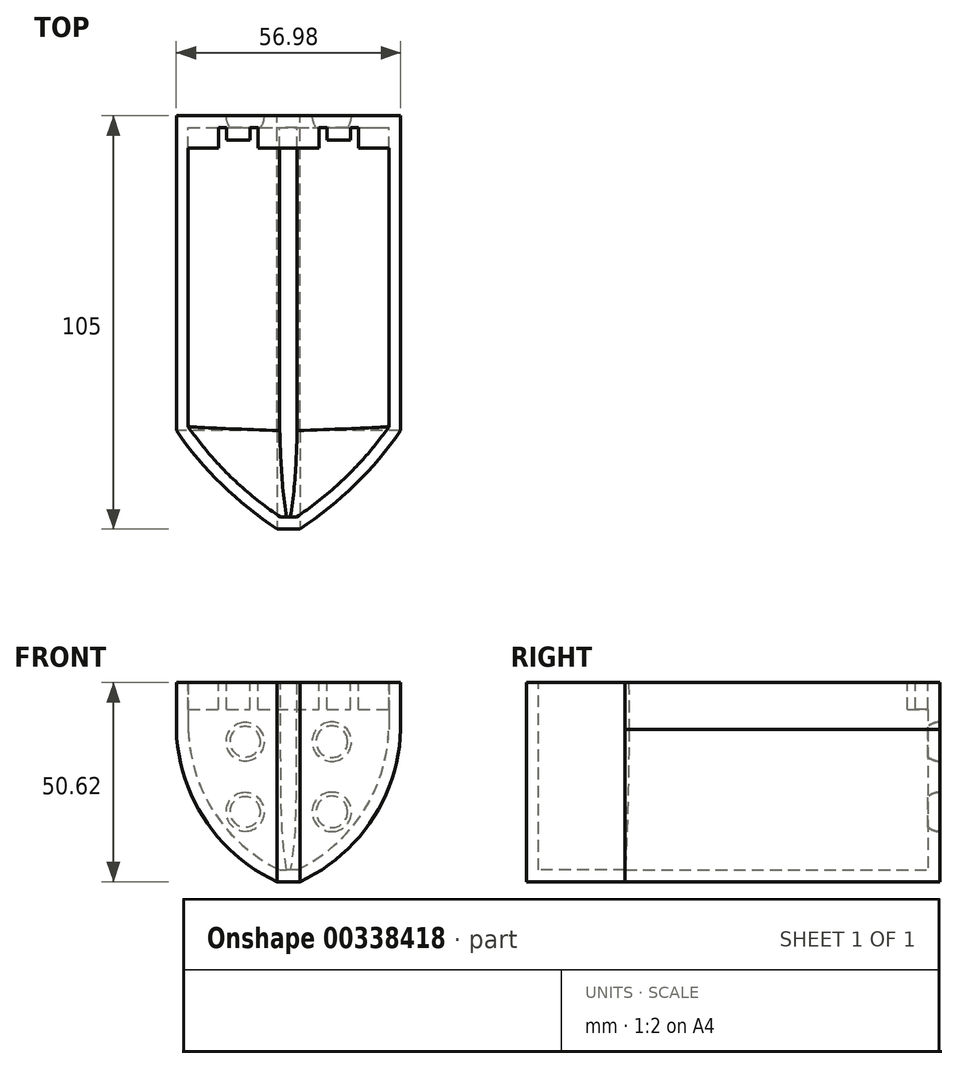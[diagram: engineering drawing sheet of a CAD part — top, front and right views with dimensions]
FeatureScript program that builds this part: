
annotation { "Feature Type Name" : "Feature", "Feature Type Description" : "" }
export const myFeature = defineFeature(function(context is Context, id is Id, definition is map)
    precondition{}
    {
        {
            var Q0;
            Q0=qCreatedBy(makeId("Front.planeOp"),FACE);
            var sketch = newSketch(context, id + "F0", { "sketchPlane" : qUnion([Q0])});
            skLineSegment(sketch, "E0.bottom", {"start": v(0, 23.95) * mm, "end": v(-28.49, 23.95) * mm});
            skLineSegment(sketch, "E0.top", {"start": v(0, -26.67) * mm, "end": v(-2.9, -26.67) * mm});
            skLineSegment(sketch, "E0.right", {"start": v(-28.49, 23.95) * mm, "end": v(-28.49, 11.98) * mm});
            skArc(sketch, "E1", {"start": v(-28.49, 11.98) * mm, "mid": v(-21.19, -10.99) * mm, "end": v(-2.9, -26.67) * mm});
            skArc(sketch, "E2.MirrorCS", {"start": v(28.49, 11.98) * mm, "mid": v(21.19, -10.99) * mm, "end": v(2.9, -26.67) * mm});
            skLineSegment(sketch, "E3.MirrorCS", {"start": v(28.49, 23.95) * mm, "end": v(28.49, 11.98) * mm});
            skLineSegment(sketch, "E4.MirrorCS", {"start": v(0, 23.95) * mm, "end": v(28.49, 23.95) * mm});
            skLineSegment(sketch, "E5.MirrorCS", {"start": v(0, -26.67) * mm, "end": v(2.9, -26.67) * mm});
            skPoint(sketch, "E6.orphan", {"position": v(-28.49, -26.67) * mm});
            skPoint(sketch, "E7.orphan", {"position": v(28.49, -26.67) * mm});
            skSolve(sketch);
        }
        {
            var Q0;
            Q0=makeQuery(id+"F0.imprint","IMPRINT",FACE,{"disambiguationData":[TD([[makeQuery(id+"F0.imprint","IMPRINT",EDGE,{"derivedFrom":sQuery(id+"F0.wireOp",EDGE,"E0.bottom")}),1.0]])]});
            extrude(context, id + "F1", {"entities" : qUnion([Q0]), "depth" : 80 * mm});
        }
        {
            var Q0;
            Q0=makeQuery(id+"F1.opExtrude","CAP_FACE",FACE,{"disambiguationData":[OSD([sQuery(id+"F0.wireOp",EDGE,"E0.bottom"),sQuery(id+"F0.wireOp",EDGE,"E0.top"),sQuery(id+"F0.wireOp",EDGE,"E0.right"),sQuery(id+"F0.wireOp",EDGE,"E1"),sQuery(id+"F0.wireOp",EDGE,"E2.MirrorCS"),sQuery(id+"F0.wireOp",EDGE,"E3.MirrorCS"),sQuery(id+"F0.wireOp",EDGE,"E4.MirrorCS"),sQuery(id+"F0.wireOp",EDGE,"E5.MirrorCS")])],"isStart":false});
            cPlane(context, id + "F2", {"entities" : qUnion([Q0]), "cplaneType" : CPlaneType.OFFSET, "offset" : 25 * mm, "width" : 150 * mm, "height" : 150 * mm});
        }
        {
            var Q0;
            Q0=qCreatedBy(id+"F2.planeOp",FACE);
            var sketch = newSketch(context, id + "F3", { "sketchPlane" : qUnion([Q0])});
            skLineSegment(sketch, "E8.bottom", {"start": v(0, -26.67) * mm, "end": v(-2.9, -26.67) * mm});
            skLineSegment(sketch, "E8.top", {"start": v(0, 23.95) * mm, "end": v(-2.9, 23.95) * mm});
            skLineSegment(sketch, "E8.right", {"start": v(-2.9, -26.67) * mm, "end": v(-2.9, 23.95) * mm});
            skLineSegment(sketch, "E9.MirrorCS", {"start": v(2.9, -26.67) * mm, "end": v(2.9, 23.95) * mm});
            skLineSegment(sketch, "E10.MirrorCS", {"start": v(0, -26.67) * mm, "end": v(2.9, -26.67) * mm});
            skLineSegment(sketch, "E11.MirrorCS", {"start": v(0, 23.95) * mm, "end": v(2.9, 23.95) * mm});
            skSolve(sketch);
        }
        {
            var Q0;
            Q0=makeQuery(id+"F1.opExtrude","SWEPT_FACE",FACE,{"disambiguationData":[OSD([sQuery(id+"F0.wireOp",EDGE,"E0.bottom"),sQuery(id+"F0.wireOp",EDGE,"E4.MirrorCS")])]});
            cPlane(context, id + "F4", {"entities" : qUnion([Q0]), "cplaneType" : CPlaneType.OFFSET, "offset" : 0 * mm, "width" : 150 * mm, "height" : 150 * mm});
        }
        {
            var Q0;
            Q0=qCreatedBy(id+"F4.planeOp",FACE);
            var sketch = newSketch(context, id + "F5", { "sketchPlane" : qUnion([Q0])});
            skArc(sketch, "E12", {"start": v(-28.49, -80) * mm, "mid": v(-16.9, -93.73) * mm, "end": v(-2.9, -105) * mm});
            skLineSegment(sketch, "E13", {"start": v(0, -105.03) * mm, "end": v(0, -80.6) * mm, "construction": true});
            skArc(sketch, "E14.MirrorCS", {"start": v(28.49, -80) * mm, "mid": v(16.9, -93.73) * mm, "end": v(2.9, -105) * mm});
            skSolve(sketch);
        }
        {
            var Q0;
            Q0=makeQuery(id+"F1.opExtrude","SWEPT_FACE",FACE,{"disambiguationData":[OSD([sQuery(id+"F0.wireOp",EDGE,"E0.top"),sQuery(id+"F0.wireOp",EDGE,"E5.MirrorCS")])]});
            cPlane(context, id + "F6", {"entities" : qUnion([Q0]), "cplaneType" : CPlaneType.OFFSET, "offset" : 0 * mm, "width" : 150 * mm, "height" : 150 * mm});
        }
        {
            var Q0;
            Q0=qCreatedBy(id+"F6.planeOp",FACE);
            var sketch = newSketch(context, id + "F7", { "sketchPlane" : qUnion([Q0])});
            skLineSegment(sketch, "E15", {"start": v(-2.9, 80) * mm, "end": v(-2.9, 105) * mm});
            skLineSegment(sketch, "E16", {"start": v(2.9, 80) * mm, "end": v(2.9, 105) * mm});
            skSolve(sketch);
        }
        {
            var Q1;
            Q1=makeQuery(id+"F1.opExtrude","CAP_FACE",FACE,{"disambiguationData":[OSD([sQuery(id+"F0.wireOp",EDGE,"E0.bottom"),sQuery(id+"F0.wireOp",EDGE,"E0.top"),sQuery(id+"F0.wireOp",EDGE,"E0.right"),sQuery(id+"F0.wireOp",EDGE,"E1"),sQuery(id+"F0.wireOp",EDGE,"E2.MirrorCS"),sQuery(id+"F0.wireOp",EDGE,"E3.MirrorCS"),sQuery(id+"F0.wireOp",EDGE,"E4.MirrorCS"),sQuery(id+"F0.wireOp",EDGE,"E5.MirrorCS")])],"isStart":false});
            var Q2;
            Q2=makeQuery(id+"F3.imprint","IMPRINT",FACE,{"disambiguationData":[TD([[makeQuery(id+"F3.imprint","IMPRINT",EDGE,{"derivedFrom":sQuery(id+"F3.wireOp",EDGE,"E8.bottom")}),-1.0]])]});
            var Q3;
            Q3=sQuery(id+"F5.wireOp",EDGE,"E12");
            var Q4;
            Q4=sQuery(id+"F5.wireOp",EDGE,"E14.MirrorCS");
            var Q5;
            Q5=sQuery(id+"F7.wireOp",EDGE,"E16");
            var Q6;
            Q6=sQuery(id+"F7.wireOp",EDGE,"E15");
            loft(context, id + "F8", {"operationType" : NewBodyOperationType.ADD, "addGuides" : true, "sheetProfilesArray" : [{ "sheetProfileEntities" : qUnion([Q1]) }, { "sheetProfileEntities" : qUnion([Q2]) }], "guidesArray" : [{ "guideEntities" : qUnion([Q3]), "guideDerivativeType" : LoftGuideDerivativeType.DEFAULT, "guideDerivativeMagnitude" : 1 }, { "guideEntities" : qUnion([Q4]), "guideDerivativeType" : LoftGuideDerivativeType.DEFAULT, "guideDerivativeMagnitude" : 1 }, { "guideEntities" : qUnion([Q5]), "guideDerivativeType" : LoftGuideDerivativeType.DEFAULT, "guideDerivativeMagnitude" : 1 }, { "guideEntities" : qUnion([Q6]), "guideDerivativeType" : LoftGuideDerivativeType.DEFAULT, "guideDerivativeMagnitude" : 1 }]});
        }
        {
            var Q0;
            {var subQ0=sQuery(id+"F0.wireOp",EDGE,"E4.MirrorCS");var subQ1=sQuery(id+"F0.wireOp",EDGE,"E0.bottom");Q0=makeQuery(id+"F8.boolean.opBoolean","MERGE",FACE,{"derivedFrom":[makeQuery(id+"F1.opExtrude","SWEPT_FACE",FACE,{"disambiguationData":[OSD([subQ1,subQ0])]}),makeQuery(id+"F8.opLoft","SWEPT_FACE",FACE,{"disambiguationData":[OSD([subQ1,subQ0,sQuery(id+"F3.wireOp",EDGE,"E8.top"),sQuery(id+"F3.wireOp",EDGE,"E11.MirrorCS"),sQuery(id+"F5.wireOp",EDGE,"E14.MirrorCS")])]})]});}
            shell(context, id + "F9", {"entities" : qUnion([Q0]), "thickness" : 3 * mm});
        }
        {
            var Q0;
            {var subQ0=sQuery(id+"F0.wireOp",EDGE,"E4.MirrorCS");var subQ1=sQuery(id+"F0.wireOp",EDGE,"E0.bottom");Q0=makeQuery(id+"F8.boolean.opBoolean","MERGE",FACE,{"derivedFrom":[makeQuery(id+"F1.opExtrude","SWEPT_FACE",FACE,{"disambiguationData":[OSD([subQ1,subQ0])]}),makeQuery(id+"F8.opLoft","SWEPT_FACE",FACE,{"disambiguationData":[OSD([subQ1,subQ0,sQuery(id+"F3.wireOp",EDGE,"E8.top"),sQuery(id+"F3.wireOp",EDGE,"E11.MirrorCS"),sQuery(id+"F5.wireOp",EDGE,"E14.MirrorCS")])]})]});}
            var sketch = newSketch(context, id + "F10", { "sketchPlane" : qUnion([Q0])});
            skLineSegment(sketch, "E17.bottom", {"start": v(-25.49, -3) * mm, "end": v(25.49, -3) * mm});
            skLineSegment(sketch, "E17.top", {"start": v(-25.49, -8.24) * mm, "end": v(25.49, -8.24) * mm});
            skLineSegment(sketch, "E17.left", {"start": v(-25.49, -3) * mm, "end": v(-25.49, -8.24) * mm});
            skLineSegment(sketch, "E17.right", {"start": v(25.49, -3) * mm, "end": v(25.49, -8.24) * mm});
            skSolve(sketch);
        }
        {
            var Q0;
            Q0=makeQuery(id+"F10.imprint","IMPRINT",FACE,{"disambiguationData":[TD([[makeQuery(id+"F10.imprint","IMPRINT",EDGE,{"derivedFrom":sQuery(id+"F10.wireOp",EDGE,"E17.bottom")}),-1.0]])]});
            extrude(context, id + "F11", {"entities" : qUnion([Q0]), "operationType" : NewBodyOperationType.ADD, "oppositeDirection" : true, "depth" : 6.8 * mm});
        }
        {
            var Q0;
            {var subQ0=sQuery(id+"F0.wireOp",EDGE,"E4.MirrorCS");var subQ1=sQuery(id+"F0.wireOp",EDGE,"E0.bottom");Q0=makeQuery(id+"F11.boolean.opBoolean","MERGE",FACE,{"derivedFrom":[makeQuery(id+"F8.boolean.opBoolean","MERGE",FACE,{"derivedFrom":[makeQuery(id+"F1.opExtrude","SWEPT_FACE",FACE,{"disambiguationData":[OSD([subQ1,subQ0])]}),makeQuery(id+"F8.opLoft","SWEPT_FACE",FACE,{"disambiguationData":[OSD([subQ1,subQ0,sQuery(id+"F3.wireOp",EDGE,"E8.top"),sQuery(id+"F3.wireOp",EDGE,"E11.MirrorCS"),sQuery(id+"F5.wireOp",EDGE,"E14.MirrorCS")])]})]}),makeQuery(id+"F11.opExtrude","CAP_FACE",FACE,{"disambiguationData":[OSD([sQuery(id+"F10.wireOp",EDGE,"E17.bottom"),sQuery(id+"F10.wireOp",EDGE,"E17.top"),sQuery(id+"F10.wireOp",EDGE,"E17.left"),sQuery(id+"F10.wireOp",EDGE,"E17.right")])],"isStart":true})]});}
            var sketch = newSketch(context, id + "F12", { "sketchPlane" : qUnion([Q0])});
            skLineSegment(sketch, "E18", {"start": v(0, 0) * mm, "end": v(0, -30.47) * mm, "construction": true});
            skPoint(sketch, "E18.endSnap0", {"position": v(0, 0) * mm});
            skLineSegment(sketch, "E19.bottom", {"start": v(-7.74, -8.24) * mm, "end": v(-17.74, -8.24) * mm});
            skLineSegment(sketch, "E19.top", {"start": v(-7.74, -3) * mm, "end": v(-9.74, -3) * mm});
            skLineSegment(sketch, "E19.left", {"start": v(-7.74, -8.24) * mm, "end": v(-7.74, -3) * mm});
            skLineSegment(sketch, "E19.right", {"start": v(-17.74, -8.24) * mm, "end": v(-17.74, -3) * mm});
            skLineSegment(sketch, "E20.top", {"start": v(-9.74, -6.24) * mm, "end": v(-15.74, -6.24) * mm});
            skLineSegment(sketch, "E20.left", {"start": v(-9.74, -3) * mm, "end": v(-9.74, -6.24) * mm});
            skLineSegment(sketch, "E20.right", {"start": v(-15.74, -3) * mm, "end": v(-15.74, -6.24) * mm});
            skLineSegment(sketch, "E21.trimOffspring", {"start": v(-15.74, -3) * mm, "end": v(-17.74, -3) * mm});
            skLineSegment(sketch, "E22.MirrorCS", {"start": v(7.74, -8.24) * mm, "end": v(7.74, -3) * mm});
            skLineSegment(sketch, "E23.MirrorCS", {"start": v(7.74, -3) * mm, "end": v(9.74, -3) * mm});
            skLineSegment(sketch, "E24.MirrorCS", {"start": v(9.74, -3) * mm, "end": v(9.74, -6.24) * mm});
            skLineSegment(sketch, "E25.MirrorCS", {"start": v(9.74, -6.24) * mm, "end": v(15.74, -6.24) * mm});
            skLineSegment(sketch, "E26.MirrorCS", {"start": v(7.74, -8.24) * mm, "end": v(17.74, -8.24) * mm});
            skLineSegment(sketch, "E27.MirrorCS", {"start": v(17.74, -8.24) * mm, "end": v(17.74, -3) * mm});
            skLineSegment(sketch, "E28.MirrorCS", {"start": v(15.74, -3) * mm, "end": v(17.74, -3) * mm});
            skLineSegment(sketch, "E29.MirrorCS", {"start": v(15.74, -3) * mm, "end": v(15.74, -6.24) * mm});
            skSolve(sketch);
        }
        {
            var Q0;
            Q0=makeQuery(id+"F12.imprint","IMPRINT",FACE,{"disambiguationData":[TD([[makeQuery(id+"F12.imprint","IMPRINT",EDGE,{"derivedFrom":sQuery(id+"F12.wireOp",EDGE,"E22.MirrorCS")}),-1.0]])]});
            var Q1;
            Q1=makeQuery(id+"F12.imprint","IMPRINT",FACE,{"disambiguationData":[TD([[makeQuery(id+"F12.imprint","IMPRINT",EDGE,{"derivedFrom":sQuery(id+"F12.wireOp",EDGE,"E19.bottom")}),1.0]])]});
            extrude(context, id + "F13", {"entities" : qUnion([Q0, Q1]), "operationType" : NewBodyOperationType.REMOVE, "oppositeDirection" : true, "depth" : 25 * mm});
        }
        {
            var Q0;
            Q0=makeQuery(id+"F1.opExtrude","CAP_FACE",FACE,{"disambiguationData":[OSD([sQuery(id+"F0.wireOp",EDGE,"E0.bottom"),sQuery(id+"F0.wireOp",EDGE,"E0.top"),sQuery(id+"F0.wireOp",EDGE,"E0.right"),sQuery(id+"F0.wireOp",EDGE,"E1"),sQuery(id+"F0.wireOp",EDGE,"E2.MirrorCS"),sQuery(id+"F0.wireOp",EDGE,"E3.MirrorCS"),sQuery(id+"F0.wireOp",EDGE,"E4.MirrorCS"),sQuery(id+"F0.wireOp",EDGE,"E5.MirrorCS")])],"isStart":true});
            var sketch = newSketch(context, id + "F14", { "sketchPlane" : qUnion([Q0])});
            skArc(sketch, "E30", {"start": v(-11, 13.92) * mm, "mid": v(-16, 8.92) * mm, "end": v(-11, 3.92) * mm});
            skLineSegment(sketch, "E31", {"start": v(-15.08, 0) * mm, "end": v(0, 0) * mm, "construction": true});
            skLineSegment(sketch, "E32", {"start": v(0, 10.01) * mm, "end": v(0, 0) * mm, "construction": true});
            skLineSegment(sketch, "E33", {"start": v(-11, 8.92) * mm, "end": v(-11, 3.92) * mm});
            skLineSegment(sketch, "E34", {"start": v(-11, 3.92) * mm, "end": v(-11, 13.92) * mm});
            skLineSegment(sketch, "E35.MirrorCS", {"start": v(-11, -3.92) * mm, "end": v(-11, -13.92) * mm});
            skArc(sketch, "E36.MirrorCS", {"start": v(-11, -13.92) * mm, "mid": v(-16, -8.92) * mm, "end": v(-11, -3.92) * mm});
            skSolve(sketch);
        }
        {
            var Q0;
            Q0=qSketchRegion(id+"F14",true);
            var Q1;
            Q1=sQuery(id+"F14.wireOp",EDGE,"E34");
            revolve(context, id + "F15", {"operationType" : NewBodyOperationType.REMOVE, "entities" : qUnion([Q0]), "axis" : qUnion([Q1]), "revolveType" : RevolveType.FULL});
        }
        {
            var Q0;
            Q0=makeQuery(id+"F1.opExtrude","CAP_FACE",FACE,{"disambiguationData":[OSD([sQuery(id+"F0.wireOp",EDGE,"E0.bottom"),sQuery(id+"F0.wireOp",EDGE,"E0.top"),sQuery(id+"F0.wireOp",EDGE,"E0.right"),sQuery(id+"F0.wireOp",EDGE,"E1"),sQuery(id+"F0.wireOp",EDGE,"E2.MirrorCS"),sQuery(id+"F0.wireOp",EDGE,"E3.MirrorCS"),sQuery(id+"F0.wireOp",EDGE,"E4.MirrorCS"),sQuery(id+"F0.wireOp",EDGE,"E5.MirrorCS")])],"isStart":true});
            var sketch = newSketch(context, id + "F16", { "sketchPlane" : qUnion([Q0])});
            skLineSegment(sketch, "E37", {"start": v(0, 0) * mm, "end": v(-9.83, 0) * mm, "construction": true});
            skLineSegment(sketch, "E38", {"start": v(0, 0) * mm, "end": v(0, 12.17) * mm, "construction": true});
            skArc(sketch, "E39.MirrorC", {"start": v(11, 13.82) * mm, "mid": v(15.9, 8.92) * mm, "end": v(11, 4.02) * mm});
            skArc(sketch, "E40.MirrorC", {"start": v(11, -13.82) * mm, "mid": v(15.9, -8.92) * mm, "end": v(11, -4.02) * mm});
            skLineSegment(sketch, "E41", {"start": v(11, 8.92) * mm, "end": v(11, 13.82) * mm});
            skLineSegment(sketch, "E42", {"start": v(11, 13.82) * mm, "end": v(11, 4.02) * mm});
            skLineSegment(sketch, "E43", {"start": v(11, -4.02) * mm, "end": v(11, -13.82) * mm});
            skSolve(sketch);
        }
        {
            var Q0;
            Q0=qSketchRegion(id+"F16",true);
            var Q1;
            Q1=sQuery(id+"F16.wireOp",EDGE,"E42");
            revolve(context, id + "F17", {"operationType" : NewBodyOperationType.REMOVE, "entities" : qUnion([Q0]), "axis" : qUnion([Q1]), "revolveType" : RevolveType.FULL, "oppositeDirection" : true});
        }
    });
